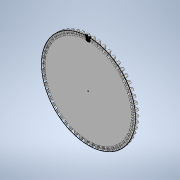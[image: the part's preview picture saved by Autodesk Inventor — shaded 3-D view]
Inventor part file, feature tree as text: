
AUTODESK INVENTOR PART (.ipt)
format: ipt  version: 2022 (Build 260153070, 153G)  size: 591,872 bytes
history: native  units: mm
features: extrude x2, sketch x1, pattern_circular x1
ambient origin geometry x8: Origin, YZ Plane, XZ Plane, XY Plane, X Axis, Y Axis, Z Axis, Center Point
bodies: Solid1 (feature_tree)
feature tree (4):
  sketch  "Sketch1"  dims[d0=3.0mm d1=0.0mm d2=10.0mm d3=0.0mm d4=540.0mm d5=360.0deg]
  extrude  "Extrusion1"  TaperAngle=0.0deg  [1 undecoded]
  extrude  "Extrusion2"  Depth=10.0mm TaperAngle=0.0deg
  pattern_circular  "Circular Pattern1"  Count=54 Angle=360.0deg
note: 1 required parameter value undecoded (feature->parameter linkage not recoverable at this tier; creation-order binding heuristic only, values carry confidence <= 0.55)
